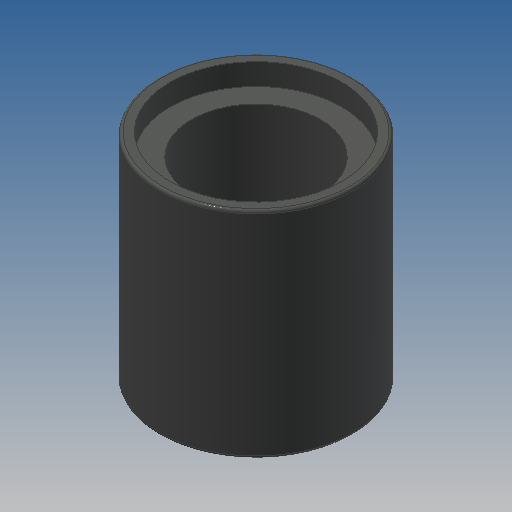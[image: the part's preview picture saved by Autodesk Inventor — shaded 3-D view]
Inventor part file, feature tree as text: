
AUTODESK INVENTOR PART (.ipt)
format: ipt  version: 2022.2 (Build 262287000, 287)  size: 145,920 bytes
history: native  units: in
note: dims shown in document units (in); Inventor stores cm internally (conversion verified against a paired STEP export)
features: revolve x1, fillet x1, sketch x1
ambient origin geometry x8: Origin, YZ Plane, XZ Plane, XY Plane, X Axis, Y Axis, Z Axis, Center Point
bodies: Solid1 (feature_tree)
feature tree (3):
  revolve  "Revolution1"  [1 undecoded]
  fillet  "Fillet1"  Radius=0.252in
  sketch  "Sketch1"  dims[d0=0.189in d1=0.315in d2=0.252in d3=0.0315in d4=0.2835in d5=90.0deg d6=0.0039in d7=0.0in d8=0.0in]
note: 1 required parameter value undecoded (feature->parameter linkage not recoverable at this tier; creation-order binding heuristic only, values carry confidence <= 0.55)
